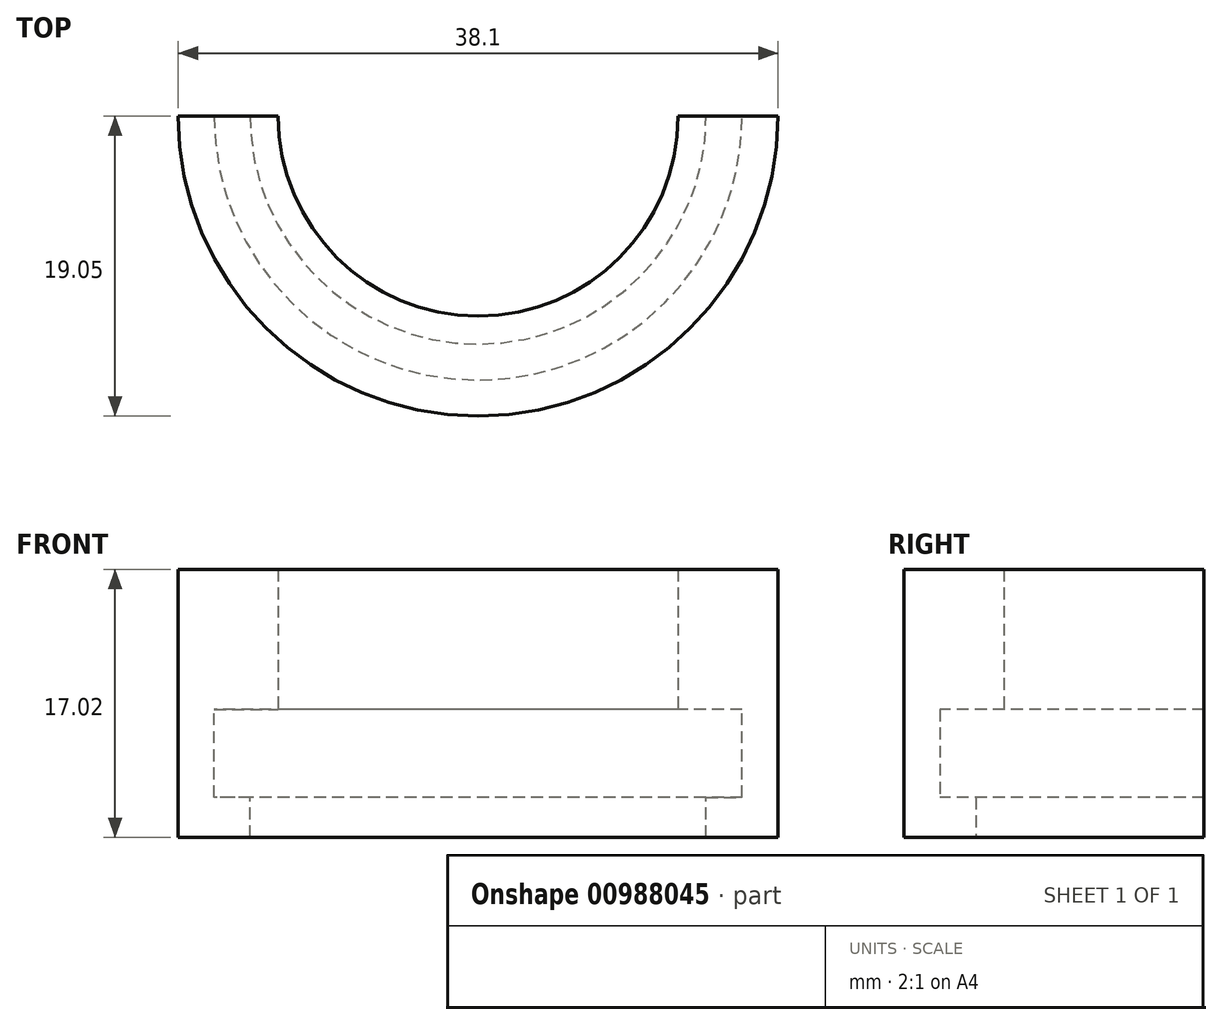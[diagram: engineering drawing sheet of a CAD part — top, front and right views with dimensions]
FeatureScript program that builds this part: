
annotation { "Feature Type Name" : "Feature", "Feature Type Description" : "" }
export const myFeature = defineFeature(function(context is Context, id is Id, definition is map)
    precondition{}
    {
        {
            var Q0;
            Q0=qCreatedBy(makeId("Front.planeOp"),FACE);
            var sketch = newSketch(context, id + "F0", { "sketchPlane" : qUnion([Q0])});
            skLineSegment(sketch, "E0", {"start": v(19.05, 0) * mm, "end": v(6.35, 0) * mm});
            skLineSegment(sketch, "E1", {"start": v(19.05, 0) * mm, "end": v(0, 0) * mm});
            skLineSegment(sketch, "E2", {"start": v(0, 0) * mm, "end": v(0, 10.67) * mm});
            skLineSegment(sketch, "E3", {"start": v(0, 10.67) * mm, "end": v(0, 17.02) * mm});
            skLineSegment(sketch, "E4", {"start": v(0, 17.02) * mm, "end": v(2.54, 17.02) * mm});
            skLineSegment(sketch, "E5", {"start": v(2.54, 17.02) * mm, "end": v(2.54, 10.67) * mm});
            skLineSegment(sketch, "E6", {"start": v(2.54, 10.67) * mm, "end": v(6.35, 10.67) * mm});
            skLineSegment(sketch, "E7", {"start": v(6.35, 10.67) * mm, "end": v(6.35, 8.13) * mm});
            skLineSegment(sketch, "E8", {"start": v(6.35, 8.13) * mm, "end": v(2.54, 8.13) * mm});
            skLineSegment(sketch, "E9", {"start": v(6.35, 10.67) * mm, "end": v(6.35, 13.2) * mm});
            skLineSegment(sketch, "E10", {"start": v(6.35, 13.2) * mm, "end": v(0, 13.2) * mm});
            skLineSegment(sketch, "E11", {"start": v(6.35, 13.2) * mm, "end": v(6.35, 11.94) * mm});
            skLineSegment(sketch, "E12", {"start": v(6.35, 11.94) * mm, "end": v(5.08, 11.94) * mm});
            skLineSegment(sketch, "E13", {"start": v(5.08, 11.94) * mm, "end": v(5.08, 13.2) * mm});
            skLineSegment(sketch, "E14", {"start": v(2.54, 17.02) * mm, "end": v(6.35, 17.02) * mm});
            skLineSegment(sketch, "E15", {"start": v(6.35, 17.02) * mm, "end": v(6.35, 13.2) * mm});
            skLineSegment(sketch, "E16", {"start": v(19.05, 0) * mm, "end": v(4.57, 0) * mm});
            skLineSegment(sketch, "E17", {"start": v(4.57, 0) * mm, "end": v(4.57, 2.54) * mm});
            skLineSegment(sketch, "E18", {"start": v(4.57, 2.54) * mm, "end": v(2.29, 2.54) * mm});
            skLineSegment(sketch, "E19", {"start": v(2.29, 2.54) * mm, "end": v(2.29, 8.13) * mm});
            skLineSegment(sketch, "E20", {"start": v(2.29, 8.13) * mm, "end": v(2.54, 8.13) * mm});
            skLineSegment(sketch, "E21", {"start": v(19.05, 0) * mm, "end": v(19.05, 4.35) * mm});
            skSolve(sketch);
        }
        {
            var Q0;
            Q0 = qSketchRegion(id + "F0", true);
            var Q1;
            Q1=sQuery(id+"F0.wireOp",EDGE,"E21");
            revolve(context, id + "F1", {"surfaceOperationType" : NewSurfaceOperationType.NEW, "entities" : qUnion([Q0]), "axis" : qUnion([Q1]), "revolveType" : RevolveType.ONE_DIRECTION, "angle" : 180 * degree});
        }
    });
